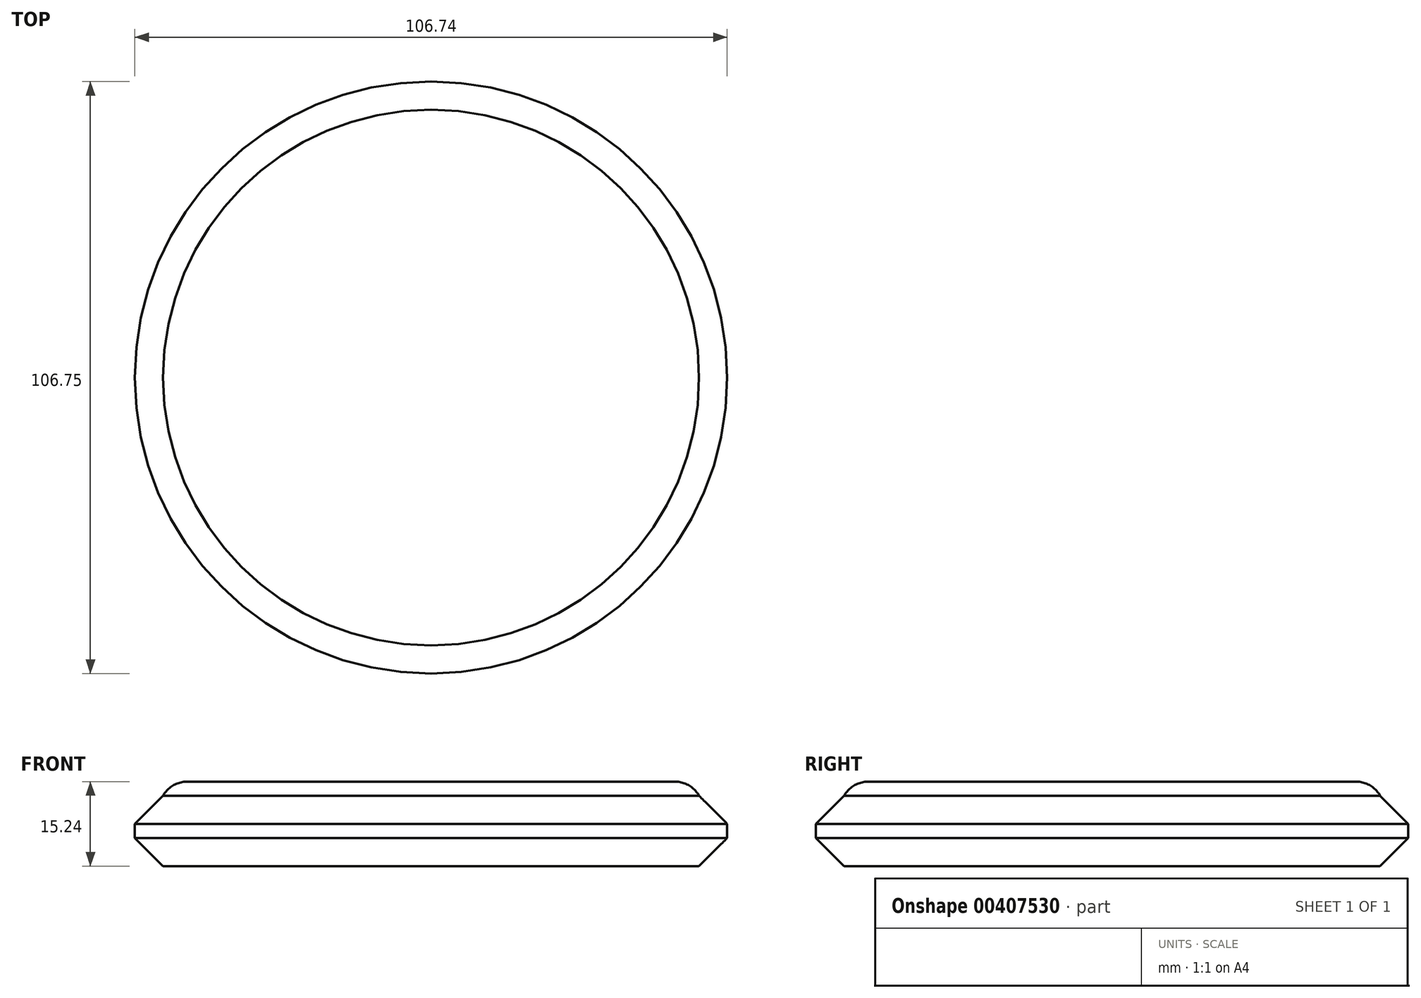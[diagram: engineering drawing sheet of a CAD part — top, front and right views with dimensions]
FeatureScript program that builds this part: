
annotation { "Feature Type Name" : "Feature", "Feature Type Description" : "" }
export const myFeature = defineFeature(function(context is Context, id is Id, definition is map)
    precondition{}
    {
        {
            var Q0;
            Q0=qCreatedBy(makeId("Top.planeOp"),FACE);
            var sketch = newSketch(context, id + "F0", { "sketchPlane" : qUnion([Q0])});
            skCircle(sketch, "E0", {"center": v(18.27, -6.34) * mm, "radius": 53.37 * mm});
            skSolve(sketch);
        }
        {
            var Q0;
            Q0 = qSketchRegion(id + "F0", true);
            extrude(context, id + "F1", {"entities" : qUnion([Q0]), "depth" : 12.7 * mm});
        }
        {
            var Q0;
            Q0=makeQuery(id+"F1.opExtrude","CAP_EDGE",EDGE,{"disambiguationData":[OSD([sQuery(id+"F0.wireOp",EDGE,"E0")])],"isStart":false});
            var Q1;
            Q1=makeQuery(id+"F1.opExtrude","CAP_EDGE",EDGE,{"disambiguationData":[OSD([sQuery(id+"F0.wireOp",EDGE,"E0")])],"isStart":true});
            var Q2;
            Q2=makeQuery(id+"F1.opExtrude","SWEPT_FACE",FACE,{"disambiguationData":[OSD([sQuery(id+"F0.wireOp",EDGE,"E0")])]});
            chamfer(context, id + "F2", {"entities" : qUnion([Q0, Q1, Q2]), "width" : 5.08 * mm, "tangentPropagation" : true});
        }
        {
            var Q0;
            Q0=makeQuery(id+"F1.opExtrude","CAP_FACE",FACE,{"disambiguationData":[OSD([sQuery(id+"F0.wireOp",EDGE,"E0")])],"isStart":false});
            extrude(context, id + "F3", {"entities" : qUnion([Q0]), "operationType" : NewBodyOperationType.ADD, "depth" : 2.54 * mm});
        }
        {
            var Q0;
            Q0=makeQuery(id+"F3.opExtrude","CAP_FACE",FACE,{"disambiguationData":[OSD([sQuery(id+"F0.wireOp",EDGE,"E0")])],"isStart":false});
            fillet(context, id + "F4", {"entities" : qUnion([Q0]), "radius" : 5.08 * mm, "tangentPropagation" : true, "allowEdgeOverflow" : false});
        }
    });
